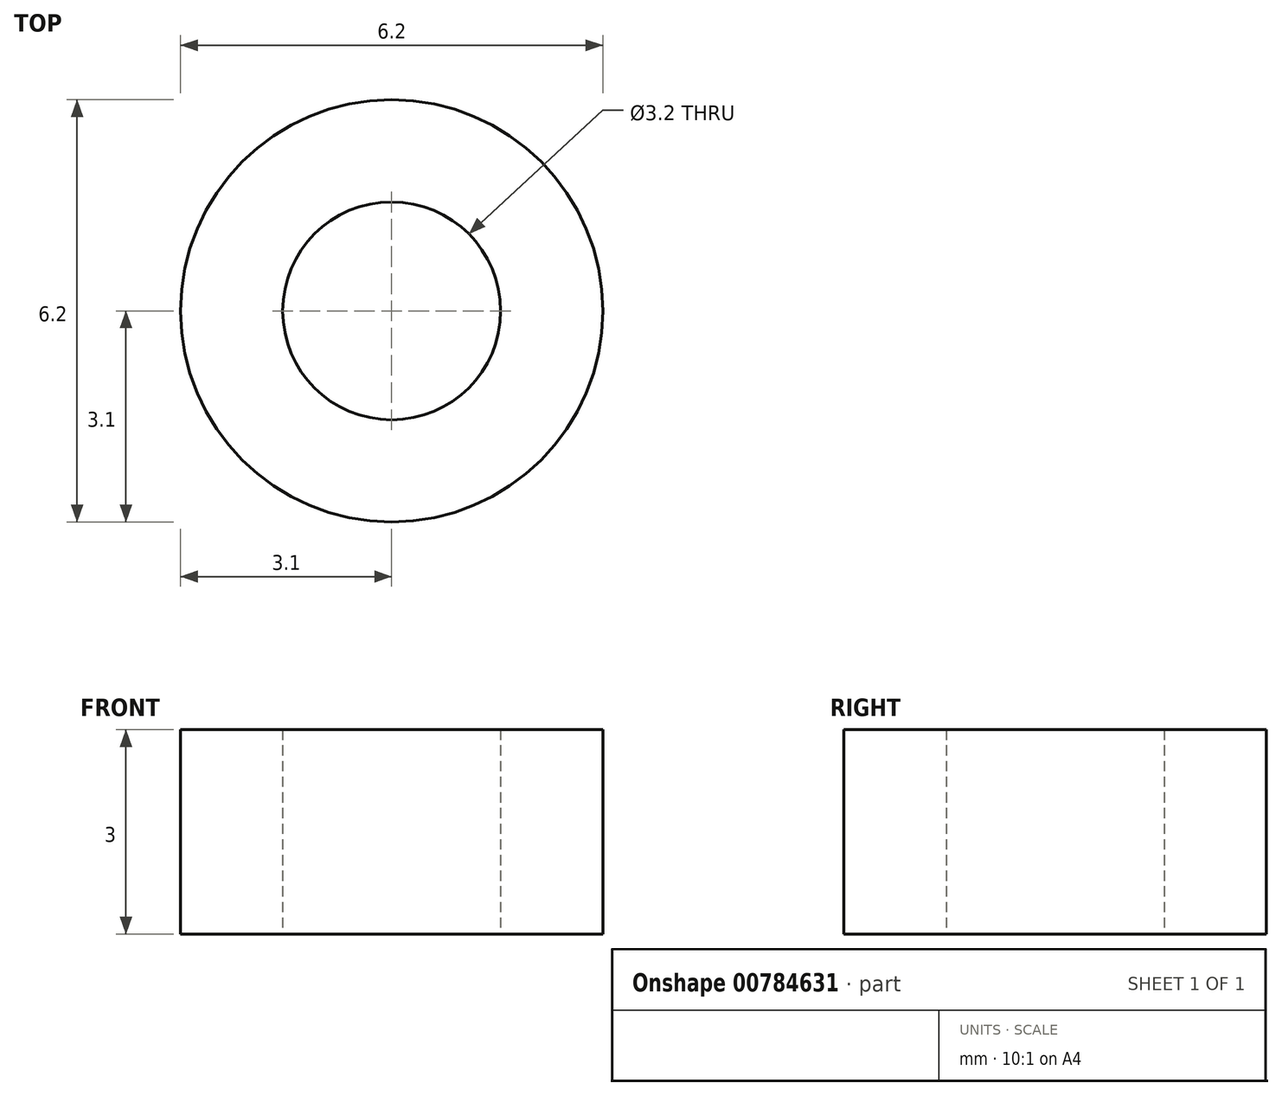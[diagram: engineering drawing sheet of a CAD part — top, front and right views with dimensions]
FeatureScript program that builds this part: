
annotation { "Feature Type Name" : "Feature", "Feature Type Description" : "" }
export const myFeature = defineFeature(function(context is Context, id is Id, definition is map)
    precondition{}
    {
        {
            var Q0;
            Q0=qCreatedBy(makeId("Top.planeOp"),FACE);
            var sketch = newSketch(context, id + "F0", { "sketchPlane" : qUnion([Q0])});
            skCircle(sketch, "E0", {"center": v(0, 0) * mm, "radius": 1.6 * mm});
            skCircle(sketch, "E1", {"center": v(0, 0) * mm, "radius": 3.1 * mm});
            skSolve(sketch);
        }
        {
            var Q0;
            Q0 = qSketchRegion(id + "F0", true);
            extrude(context, id + "F1", {"entities" : qUnion([Q0]), "depth" : 3 * mm, "offsetDistance" : 25 * mm});
        }
    });
